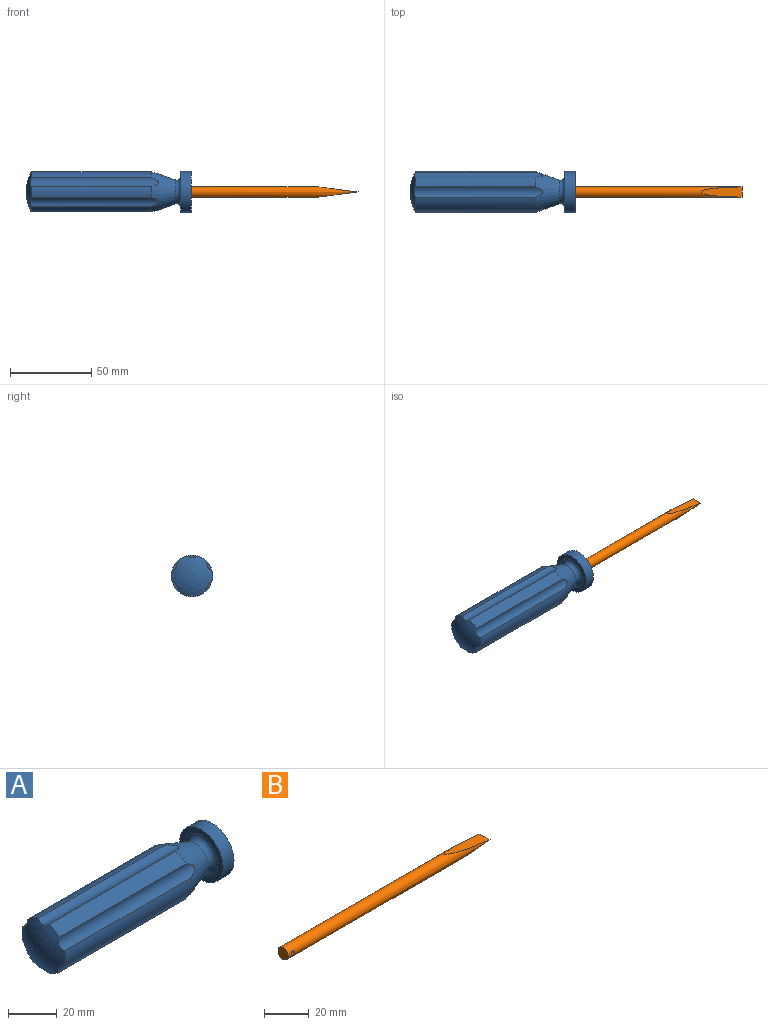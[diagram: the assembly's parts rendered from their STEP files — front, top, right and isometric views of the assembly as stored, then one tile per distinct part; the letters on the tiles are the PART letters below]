
ASSEMBLY  parts=2 mates=1
PART A: 21 faces, bbox 101.6x25.4x25.4 mm
  f0: cylinder r=12.7mm len=73.76mm, axis (1,0,0), area 517.2mm2, adj f11,f13,f18,f19
  f1: cylinder r=12.7mm len=73.76mm, axis (1,0,0), area 517.2mm2, adj f11,f13,f17,f18
  f2: cylinder r=12.7mm len=73.76mm, axis (1,0,0), area 517.2mm2, adj f11,f13,f16,f17
  f3: cylinder r=12.7mm len=73.76mm, axis (1,0,0), area 517.2mm2, adj f11,f13,f15,f16
  f4: cylinder r=12.7mm len=73.76mm, axis (1,0,0), area 517.2mm2, adj f11,f13,f14,f15
  f5: plane 6.35x6.35mm, normal (1,0,0), area 31.7mm2, adj f6
  f6: cylinder r=3.17mm len=24.38mm, axis (1,0,0), area 486.4mm2, adj f5,f7
  f7: plane 25.4x25.4mm, normal (1,0,0), area 475mm2, adj f6,f8
  f8: cylinder r=12.7mm len=25.4mm, axis (1,0,0), area 506.7mm2, adj f7,f9
  f9: plane 25.4x25.4mm, normal (-1,0,0), area 207.2mm2, adj f8,f10
  f10: torus R=9.76mm, axis (1,0,0), area 244.8mm2, adj f9,f11
  f11: cone r=7.38mm half-angle=20deg, axis (-1,0,0), area 868.4mm2, adj f0,f1,f2,f3,f4,f10,f12,f14
  f12: cylinder r=12.7mm len=73.76mm, axis (1,0,0), area 517.2mm2, adj f11,f13,f14,f19
  f13: sphere r=25.04mm, area 500.1mm2, adj f0,f1,f2,f3,f4,f12,f14,f15
  f14: cylinder r=4.83mm len=78.77mm, axis (1,0,0), area 521mm2, adj f4,f11,f12,f13
  f15: cylinder r=4.83mm len=78.77mm, axis (1,0,0), area 521mm2, adj f3,f4,f11,f13
  f16: cylinder r=4.83mm len=78.77mm, axis (1,0,0), area 521mm2, adj f2,f3,f11,f13
  f17: cylinder r=4.83mm len=78.77mm, axis (1,0,0), area 521mm2, adj f1,f2,f11,f13
  f18: cylinder r=4.83mm len=78.77mm, axis (1,0,0), area 521mm2, adj f0,f1,f11,f13
  f19: cylinder r=4.83mm len=78.77mm, axis (1,0,0), area 521mm2, adj f0,f11,f12,f13
  f20: sphere r=1.19mm, area 17.9mm2
PART B: 5 faces, bbox 127x6.4x6.4 mm
  f0: cylinder r=3.17mm len=127mm, axis (1,0,0), area 2204.9mm2, adj f1,f2,f3,f4
  f1: plane 6.35x6.35mm, normal (-1,0,0), area 31.7mm2, adj f0
  f2: plane 25.16x6.35mm, normal (0.13,0,-0.99), area 126.5mm2, adj f0,f4
  f3: cylinder r=1.19mm len=6.35mm, axis (0,-1,0), area 45.9mm2, adj f0
  f4: plane 25.16x6.35mm, normal (0.13,0,0.99), area 126.5mm2, adj f0,f2
PLACE A t=(-37.45,-4.75,6.56)mm
PLACE B t=(98.44,-4.75,6.56)mm
MATE planar B.f0 <-> A.f0  axis (-1,0,0) through (-28.56,-4.75,6.56)mm
